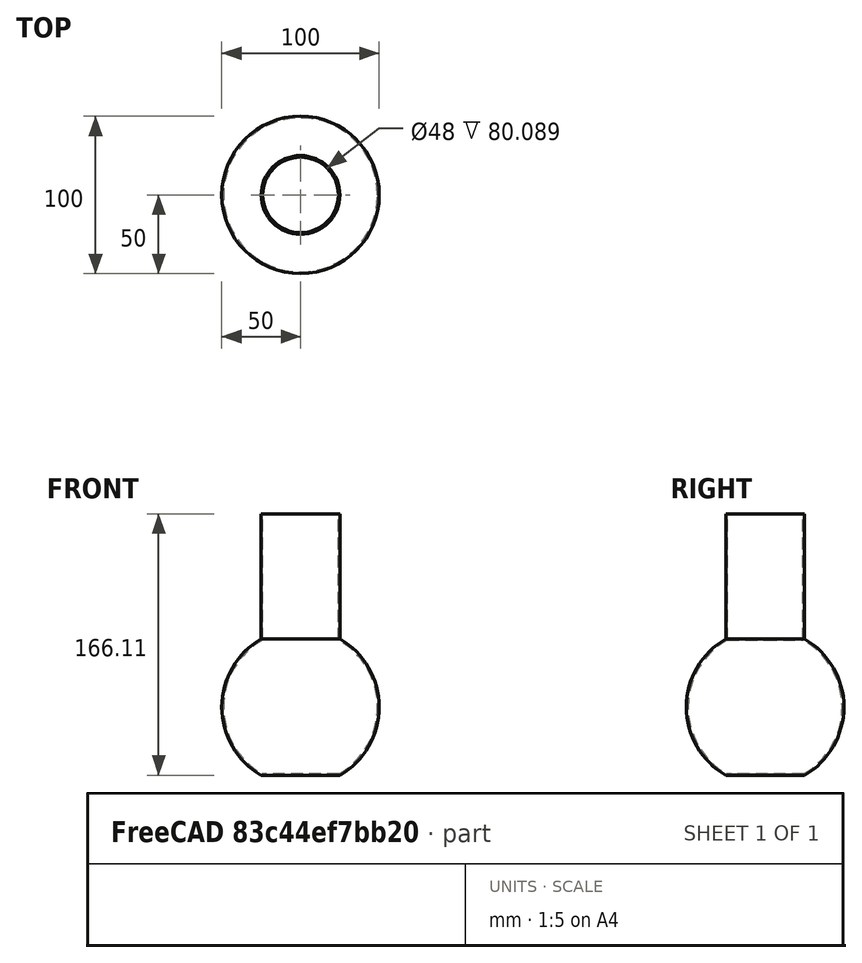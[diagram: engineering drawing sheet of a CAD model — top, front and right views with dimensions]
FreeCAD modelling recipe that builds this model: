
FCSTD DOCUMENT  (FreeCAD 0.19R)
Label: ERLENMEYER-01
License: Creative Commons Attribution-NonCommercial
LicenseURL: http://creativecommons.org/licenses/by-nc/4.0/
objects: Sketcher::SketchObject×1, Part::Revolution×1
note: 2 computed .brp shape members not serialized (recipe doc carries the construction recipe); baked Part::Feature solids carry a one-line shape summary decoded from their .brp

FEATURE [Sketcher::SketchObject] Sketch
  Placement = pos=(0,0,0) rot=(1,0,0;1.5708rad)
  sketch-geometry (12):
    g0: ArcOfCircle CenterX=0 CenterY=0 CenterZ=0 NormalX=0 NormalY=0 NormalZ=1 AngleXU=0 Radius=50 StartAngle=5.23599 EndAngle=7.33038
    g1: LineSegment [constr] StartX=0 StartY=42.72 StartZ=0 EndX=0 EndY=-42.4352 EndZ=0
    g2: LineSegment [constr] StartX=24 StartY=42.72 StartZ=0 EndX=0 EndY=42.72 EndZ=0
    g3: LineSegment [constr] StartX=0 StartY=0 StartZ=0 EndX=25 EndY=43.3013 EndZ=0
    g4: LineSegment [constr] StartX=0 StartY=0 StartZ=0 EndX=25 EndY=-43.3013 EndZ=0
    g5: ArcOfCircle CenterX=0 CenterY=0 CenterZ=0 NormalX=0 NormalY=0 NormalZ=1 AngleXU=0 Radius=49 StartAngle=5.23599 EndAngle=7.34213
    g6: LineSegment StartX=24.5 StartY=-42.4352 StartZ=0 EndX=0 EndY=-42.4352 EndZ=0
    g7: LineSegment StartX=0 StartY=-43.3013 StartZ=0 EndX=25 EndY=-43.3013 EndZ=0
    g8: LineSegment StartX=0 StartY=-42.4352 StartZ=0 EndX=0 EndY=-43.3013 EndZ=0
    g9: LineSegment StartX=24 StartY=42.72 StartZ=0 EndX=24 EndY=122.809 EndZ=0
    g10: LineSegment StartX=24 StartY=122.809 StartZ=0 EndX=25 EndY=122.809 EndZ=0
    g11: LineSegment StartX=25 StartY=122.809 StartZ=0 EndX=25 EndY=43.3013 EndZ=0
  constraints (30):
    c: Coincident(g0,g-1)
    c: Horizontal(g2)
    c: Coincident(g2,g1)
    c: Coincident(g3,g0)
    c: Coincident(g3,g0)
    c: Coincident(g4,g0)
    c: Coincident(g0,g4)
    c: Angle(g3) = 1.0472
    c: Angle(g4) = -1.0472
    c: Radius(g0) = 50
    c: Coincident(g5,g0)
    c: Radius(g5) = 49
    c: Coincident(g2,g5)
    c: PointOnObject(g5,g4)
    c: Coincident(g6,g5)
    c: Horizontal(g6)
    c: PointOnObject(g7,g-2)
    c: Coincident(g7,g0)
    c: Horizontal(g7)
    c: PointOnObject(g1,g6)
    c: Coincident(g8,g6)
    c: Coincident(g8,g7)
    c: Vertical(g8)
    c: Coincident(g9,g10)
    c: Coincident(g10,g11)
    c: Horizontal(g10)
    c: Vertical(g9)
    c: Vertical(g11)
    c: DistanceX(g5,g0) = 1
    c: Coincident(g2,g9)
FEATURE [Part::Revolution] Revolve
  Angle = 360
  Axis = (0,0,1)
  Base = (0,0,0)
  FaceMakerClass = Part::FaceMakerBullseye
  Solid = true
  Source = -> Sketch
  Symmetric = false
